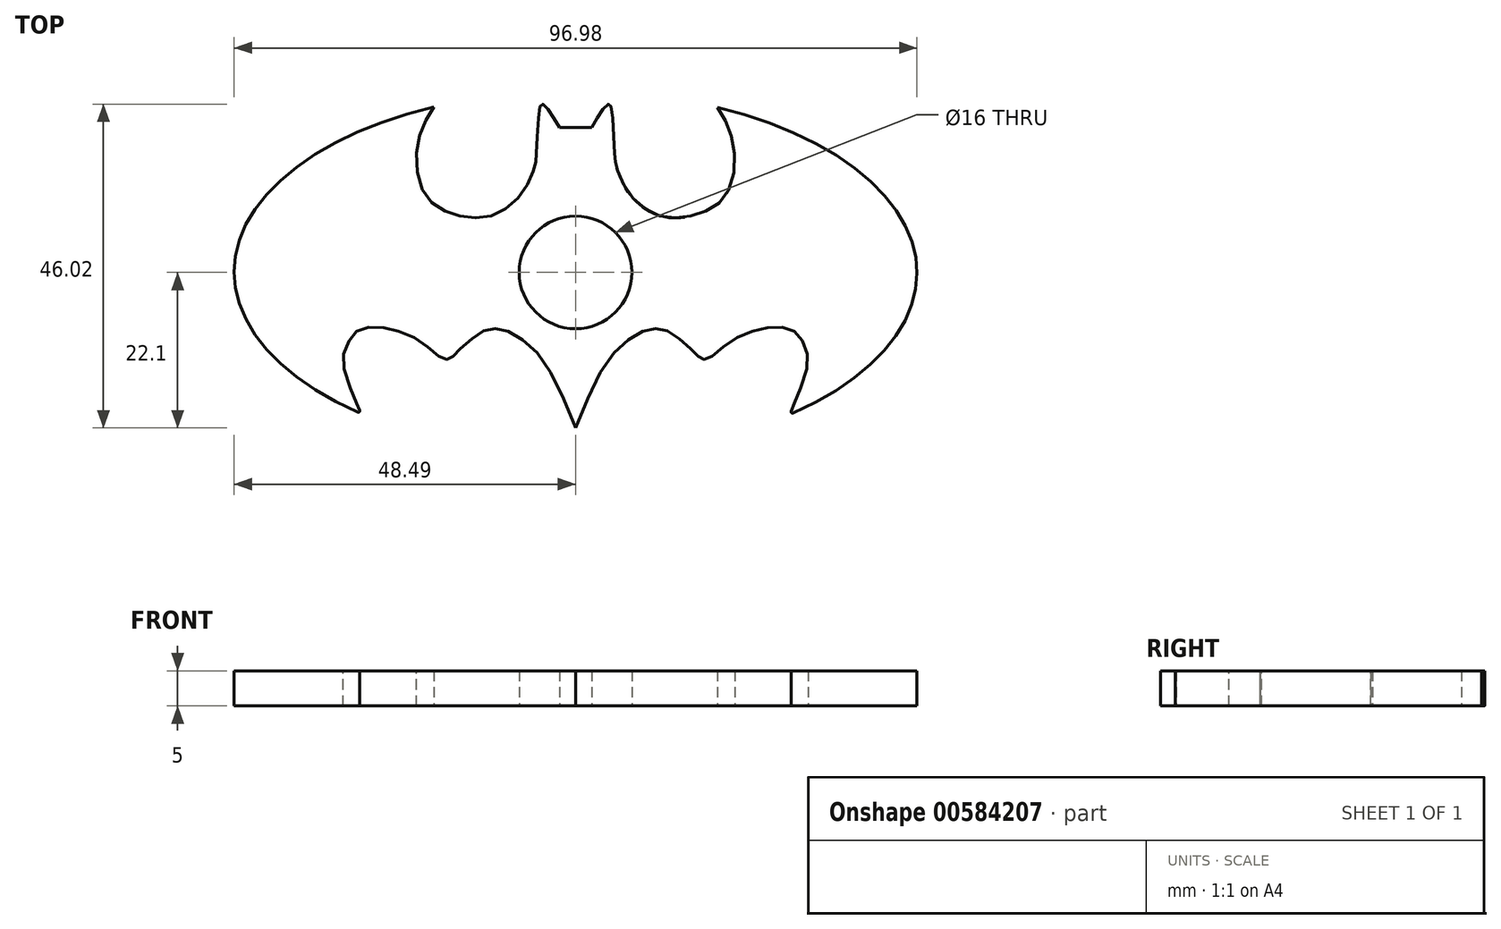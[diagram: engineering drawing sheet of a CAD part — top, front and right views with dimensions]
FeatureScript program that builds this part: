
annotation { "Feature Type Name" : "Feature", "Feature Type Description" : "" }
export const myFeature = defineFeature(function(context is Context, id is Id, definition is map)
    precondition{}
    {
        {
            var Q0;
            Q0=qCreatedBy(makeId("Top.planeOp"),FACE);
            var sketch = newSketch(context, id + "F0", { "sketchPlane" : qUnion([Q0])});
            skFitSpline(sketch, "E0", {"points": [v(-20.13, 25.53) * mm, v(-22.4, 20.3) * mm, v(-21.48, 13.2) * mm, v(-17.16, 10.23) * mm, v(-11.9, 10.06) * mm, v(-7.42, 13.53) * mm, v(-5.72, 17.34) * mm, v(-5.56, 18.65) * mm, v(-5.19, 24.8) * mm, v(-4.86, 25.88) * mm, v(-4.6, 25.88) * mm, v(-3.62, 24.77) * mm, v(-2.28, 22.62) * mm], "startDerivative": vector(-26.09, -43.9) * mm, "endDerivative": vector(18.16, -30.92) * mm});
            skLineSegment(sketch, "E1", {"start": v(-2.28, 22.62) * mm, "end": v(0, 22.62) * mm});
            skFitSpline(sketch, "E2", {"points": [v(0, -20.1) * mm, v(-4.34, -10.9) * mm, v(-7.78, -7.38) * mm, v(-10.33, -6.1) * mm, v(-12.12, -6.03) * mm, v(-13.84, -6.78) * mm, v(-15.94, -8.5) * mm, v(-17.21, -9.7) * mm, v(-17.67, -10.17) * mm, v(-18.2, -10.36) * mm, v(-18.79, -10.28) * mm, v(-20.17, -9.27) * mm, v(-22.6, -7.46) * mm, v(-25.6, -6.23) * mm, v(-28.2, -5.75) * mm, v(-30.53, -6.1) * mm, v(-31.73, -7.02) * mm, v(-32.8, -9.16) * mm, v(-32.93, -11.45) * mm, v(-31.45, -15.7) * mm, v(-30.73, -17.4) * mm], "startDerivative": vector(-40.15, 99.8) * mm, "endDerivative": vector(13.96, -32.46) * mm});
            skPoint(sketch, "E3.first.point", {"position": v(-31.67, -17.2) * mm});
            skPoint(sketch, "E3.second.point", {"position": v(-31.08, -16.59) * mm});
            skPoint(sketch, "E3.third.point", {"position": v(-31.08, -16.59) * mm});
            skLineSegment(sketch, "E4", {"start": v(0, 22.62) * mm, "end": v(0, -25.87) * mm, "construction": true});
            skLineSegment(sketch, "E5.MirrorCS", {"start": v(2.28, 22.62) * mm, "end": v(0, 22.62) * mm});
            skPoint(sketch, "E6.MirrorP", {"position": v(31.08, -16.59) * mm});
            skFitSpline(sketch, "E7.MirrorCS", {"points": [v(0, -20.1) * mm, v(4.34, -10.9) * mm, v(7.78, -7.38) * mm, v(10.33, -6.1) * mm, v(12.12, -6.03) * mm, v(13.84, -6.78) * mm, v(15.94, -8.5) * mm, v(17.21, -9.7) * mm, v(17.67, -10.17) * mm, v(18.2, -10.36) * mm, v(18.79, -10.28) * mm, v(20.17, -9.27) * mm, v(22.6, -7.46) * mm, v(25.6, -6.23) * mm, v(28.2, -5.75) * mm, v(30.53, -6.1) * mm, v(31.73, -7.02) * mm, v(32.8, -9.16) * mm, v(32.93, -11.45) * mm, v(31.45, -15.7) * mm, v(30.73, -17.4) * mm], "startDerivative": vector(40.15, 99.8) * mm, "endDerivative": vector(-13.96, -32.46) * mm});
            skPoint(sketch, "E8.MirrorP", {"position": v(31.67, -17.2) * mm});
            skFitSpline(sketch, "E9.MirrorCS", {"points": [v(20.13, 25.53) * mm, v(22.4, 20.3) * mm, v(21.48, 13.2) * mm, v(17.16, 10.23) * mm, v(11.9, 10.06) * mm, v(7.42, 13.53) * mm, v(5.72, 17.34) * mm, v(5.56, 18.65) * mm, v(5.19, 24.8) * mm, v(4.86, 25.88) * mm, v(4.6, 25.88) * mm, v(3.62, 24.77) * mm, v(2.28, 22.62) * mm], "startDerivative": vector(26.09, -43.9) * mm, "endDerivative": vector(-18.16, -30.92) * mm});
            skCircle(sketch, "E10", {"center": v(0, 2) * mm, "radius": 8 * mm});
            skLineSegment(sketch, "E11", {"start": v(-48.5, 2.1) * mm, "end": v(48.5, 2.1) * mm, "construction": true});
            skEllipticalArc(sketch, "E12", {});
            skLineSegment(sketch, "E13", {"start": v(-31.08, -16.59) * mm, "end": v(-30.65, -17.6) * mm});
            skEllipticalArc(sketch, "E14.trimOffspring", {});
            skPoint(sketch, "E15.visualSharp", {"position": v(-30.45, -18.07) * mm});
            skArc(sketch, "E15.filletArc", {"start": v(-30.91, -17.86) * mm, "mid": v(-30.69, -17.82) * mm, "end": v(-30.65, -17.6) * mm});
            skLineSegment(sketch, "E16", {"start": v(31.08, -16.59) * mm, "end": v(30.61, -17.7) * mm});
            skPoint(sketch, "E17.visualSharp", {"position": v(30.42, -18.16) * mm});
            skArc(sketch, "E17.filletArc", {"start": v(30.61, -17.7) * mm, "mid": v(30.66, -17.93) * mm, "end": v(30.88, -17.97) * mm});
            const initialGuessF0  = {"E12": [0, 0.002, -0.9999979750292427, 0.002012445630099361, 0.048492257889837395, 0.02583750383918345, 5.14158624500311, 0.8807092972419206], "E14.trimOffspring": [0, 0.002, -0.9999979750292427, 0.002012445630099361, 0.048492257889837395, 0.02583750383918345, 2.262116125750283, 4.284421521285877]};
            skSetInitialGuess(sketch, initialGuessF0);
            skSolve(sketch);
        }
        {
            var Q0;
            Q0=qSketchRegion(id+"F0",true);
            extrude(context, id + "F1", {"entities" : qUnion([Q0]), "depth" : 5 * mm});
        }
        {
            var Q0;
            Q0=makeQuery(id+"F1.opExtrude","CAP_FACE",FACE,{"disambiguationData":[OSD([sQuery(id+"F0.wireOp",EDGE,"E0"),sQuery(id+"F0.wireOp",EDGE,"E1"),sQuery(id+"F0.wireOp",EDGE,"E2"),sQuery(id+"F0.wireOp",EDGE,"E5.MirrorCS"),sQuery(id+"F0.wireOp",EDGE,"E7.MirrorCS"),sQuery(id+"F0.wireOp",EDGE,"E9.MirrorCS"),sQuery(id+"F0.wireOp",EDGE,"E10"),sQuery(id+"F0.wireOp",EDGE,"E12"),sQuery(id+"F0.wireOp",EDGE,"E13"),sQuery(id+"F0.wireOp",EDGE,"E14.trimOffspring"),sQuery(id+"F0.wireOp",EDGE,"E15.filletArc"),sQuery(id+"F0.wireOp",EDGE,"E16"),sQuery(id+"F0.wireOp",EDGE,"E17.filletArc")])],"isStart":false});
            var sketch = newSketch(context, id + "F2", { "sketchPlane" : qUnion([Q0])});
            skLineSegment(sketch, "E18", {"start": v(-3.81, 21.13) * mm, "end": v(-7.1, 9.91) * mm});
            skLineSegment(sketch, "E19", {"start": v(-7.1, 9.91) * mm, "end": v(-1.68, 10.88) * mm});
            skLineSegment(sketch, "E20", {"start": v(-1.68, 10.88) * mm, "end": v(3.05, 10.6) * mm});
            skLineSegment(sketch, "E21", {"start": v(3.05, 10.6) * mm, "end": v(6.92, 9.33) * mm});
            skLineSegment(sketch, "E22", {"start": v(6.92, 9.33) * mm, "end": v(5.86, 13.59) * mm});
            skLineSegment(sketch, "E23", {"start": v(5.86, 13.59) * mm, "end": v(4.12, 20.94) * mm});
            skLineSegment(sketch, "E24", {"start": v(4.12, 20.94) * mm, "end": v(-3.81, 21.13) * mm});
            skLineSegment(sketch, "E25", {"start": v(-3.04, -7.49) * mm, "end": v(3.92, -7.59) * mm});
            skLineSegment(sketch, "E26", {"start": v(3.92, -7.59) * mm, "end": v(0.35, -15.22) * mm});
            skLineSegment(sketch, "E27", {"start": v(0.35, -15.22) * mm, "end": v(-3.42, -8.84) * mm});
            skLineSegment(sketch, "E28", {"start": v(-3.42, -8.84) * mm, "end": v(-3.04, -7.49) * mm});
            skSolve(sketch);
        }
        {
            var Q0;
            Q0=qSketchRegion(id+"F2",true);
            var Q1;
            Q1=makeQuery(id+"FE2FyxEvqymzPK9_1.opShell","OFFSET_FACE",FACE,{"disambiguationData":[OSD([sQuery(id+"F0.wireOp",EDGE,"E0"),sQuery(id+"F0.wireOp",EDGE,"E1"),sQuery(id+"F0.wireOp",EDGE,"E2"),sQuery(id+"F0.wireOp",EDGE,"E5.MirrorCS"),sQuery(id+"F0.wireOp",EDGE,"E7.MirrorCS"),sQuery(id+"F0.wireOp",EDGE,"E9.MirrorCS"),sQuery(id+"F0.wireOp",EDGE,"E10"),sQuery(id+"F0.wireOp",EDGE,"E12"),sQuery(id+"F0.wireOp",EDGE,"E13"),sQuery(id+"F0.wireOp",EDGE,"E14.trimOffspring"),sQuery(id+"F0.wireOp",EDGE,"E15.filletArc"),sQuery(id+"F0.wireOp",EDGE,"E16"),sQuery(id+"F0.wireOp",EDGE,"E17.filletArc")]),OD(2.0)]});
            extrude(context, id + "F3", {"entities" : qUnion([Q0]), "operationType" : NewBodyOperationType.ADD, "oppositeDirection" : true, "endBoundEntityFace" : qUnion([Q1]), "depth" : 4 * mm});
        }
    });
